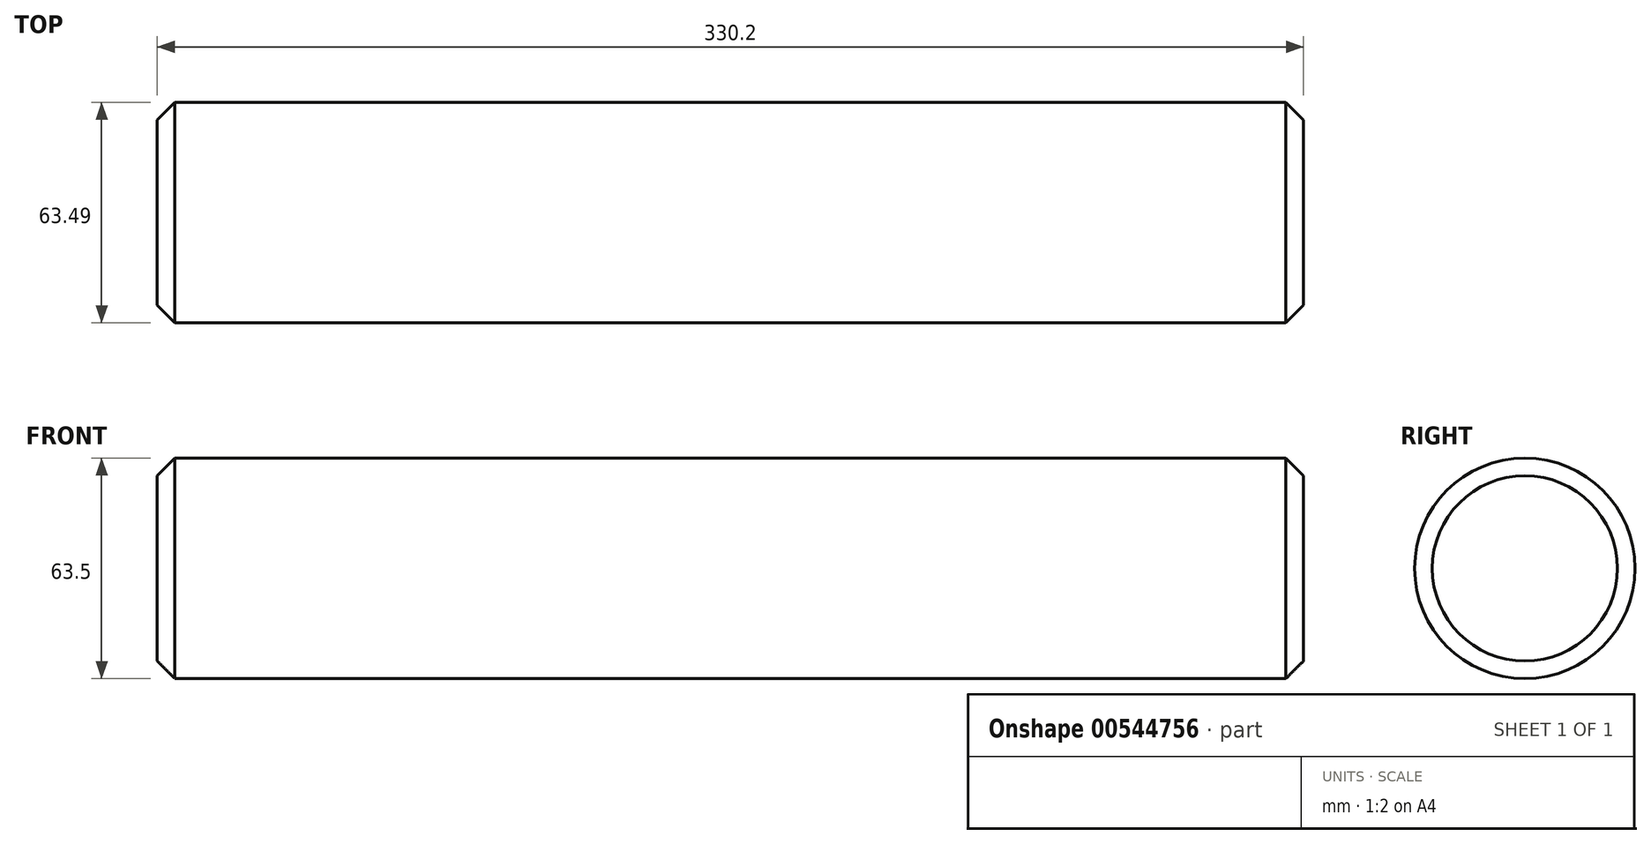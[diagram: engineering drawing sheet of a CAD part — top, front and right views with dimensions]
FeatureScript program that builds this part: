
annotation { "Feature Type Name" : "Feature", "Feature Type Description" : "" }
export const myFeature = defineFeature(function(context is Context, id is Id, definition is map)
    precondition{}
    {
        {
            var Q0;
            Q0=qCreatedBy(makeId("Right.planeOp"),FACE);
            var sketch = newSketch(context, id + "F0", { "sketchPlane" : qUnion([Q0])});
            skCircle(sketch, "E0", {"center": v(-221.23, 305.68) * mm, "radius": 31.75 * mm});
            skSolve(sketch);
        }
        {
            var Q0;
            Q0=makeQuery(id+"F0.imprint","IMPRINT",FACE,{"disambiguationData":[TD([[makeQuery(id+"F0.imprint","IMPRINT",EDGE,{"derivedFrom":sQuery(id+"F0.wireOp",EDGE,"E0")}),1.0]])]});
            extrude(context, id + "F1", {"entities" : qUnion([Q0]), "depth" : 330.2 * mm, "offsetDistance" : 25.4 * mm});
        }
        {
            var Q0;
            Q0=makeQuery(id+"F1.opExtrude","CAP_EDGE",EDGE,{"disambiguationData":[OSD([sQuery(id+"F0.wireOp",EDGE,"E0")])],"isStart":false});
            var Q1;
            Q1=makeQuery(id+"F1.opExtrude","CAP_EDGE",EDGE,{"disambiguationData":[OSD([sQuery(id+"F0.wireOp",EDGE,"E0")])],"isStart":true});
            chamfer(context, id + "F2", {"entities" : qUnion([Q0, Q1]), "width" : 5.08 * mm, "tangentPropagation" : true});
        }
    });
